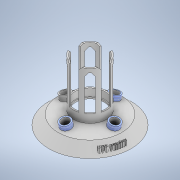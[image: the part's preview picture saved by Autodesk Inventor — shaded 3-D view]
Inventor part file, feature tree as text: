
AUTODESK INVENTOR PART (.ipt)
format: ipt  version: 2022.4 (Build 264492010, 492A)  size: 885,248 bytes
history: native  units: in
note: dims shown in document units (in); Inventor stores cm internally (conversion verified against a paired STEP export)
features: sketch x11, extrude x7, revolve x4, pattern_circular x4, plane x1, emboss x1, projected_geometry x1
ambient origin geometry x8: Origin, YZ Plane, XZ Plane, XY Plane, X Axis, Y Axis, Z Axis, Center Point
bodies: Solid1 (feature_tree)
feature tree (29):
  extrude  "Extrusion1"  Depth=0.0964in
  revolve  "Revolution1"  [1 undecoded]
  plane  "Work Plane1"
  extrude  "Extrusion3"  Depth=2.3622in
  extrude  "Extrusion4"  TaperAngle=0.0deg  [1 undecoded]
  extrude  "Extrusion5"  Depth=2.3622in
  revolve  "Revolution2"  [1 undecoded]
  pattern_circular  "Circular Pattern1"  Count=10  [1 undecoded]
  extrude  "Extrusion6"  TaperAngle=360.0deg  [1 undecoded]
  pattern_circular  "Circular Pattern2"  Count=8 Angle=360.0deg
  extrude  "Extrusion7"  TaperAngle=0.0deg  [1 undecoded]
  revolve  "Revolution3"  [1 undecoded]
  revolve  "Revolution4"  [1 undecoded]
  pattern_circular  "Number of vials"  [2 undecoded]
  extrude  "Extrusion8"  Depth=4.626in
  pattern_circular  "Circular Pattern4"  [2 undecoded]
  emboss  "Emboss4"
  sketch  "Sketch1"  dims[d2=0.1969in d3=0.0in d8=0.0964in]
  sketch  "Sketch4"  dims[d9=90.0deg d10=0.5315in]
  sketch  "Sketch5"  dims[d11=2.5984in d12=2.3622in]
  sketch  "Sketch6"  dims[d13=0.1969in d14=0.0in d15=0.0in]
  sketch  "Sketch7"  dims[d16=2.5197in d17=2.3622in]
  sketch  "Sketch9"  dims[d18=0.0787in d19=0.0in d22=0.1181in d23=3.937in d24=0.0in]
  sketch  "Sketch13"  dims[d25=0.0591in d26=0.0in d36=360.0deg]
  sketch  "Sketch14"  dims[d38=360.0deg]
  sketch  "Sketch16"  dims[d40=5.2756in]
  sketch  "Sketch17"  dims[d43=0.0in d44=0.0in d45=3.1496in d46=360.0deg]
  sketch  "Sketch20"  dims[d49=0.5906in d50=0.0in d51=0.6299in d52=4.5669in d53=5.0591in d54=4.626in d55=0.1575in d56=0.0in d60=0.1969in d61=0.1969in d62=0.1969in d63=90.0deg d72=360.0deg d78=360.0deg d81=0.5906in d82=0.0in d83=0.7874in d85=4.3319in d86=0.0in d87=1.5748in d88=360.0deg d98=0.0787in d102=0.315in d103=0.1969in d104=0.1969in d106=0.1969in d107=0.1969in d108=0.0787in d109=0.0in d110=0.315in d111=2.6772in d112=2.6772in d113=0.0787in d117=0.6202in d118=0.3438in d68=0.0344in d69=0.0344in d73=0.0344in]
  projected_geometry  "Project Cut Edges1"
note: 12 required parameter values undecoded (feature->parameter linkage not recoverable at this tier; creation-order binding heuristic only, values carry confidence <= 0.55)